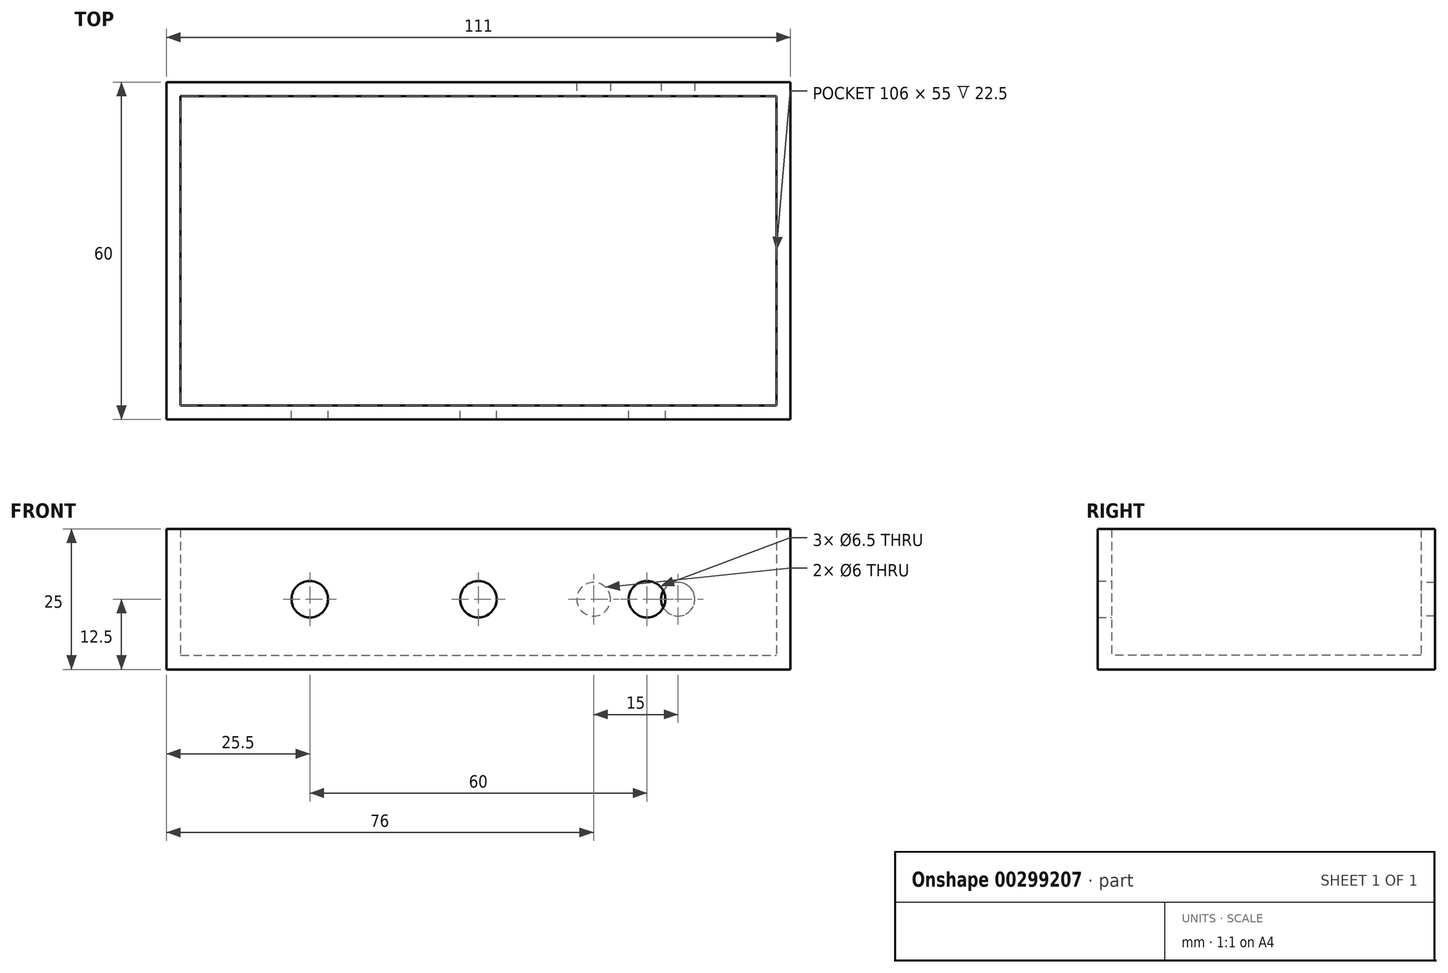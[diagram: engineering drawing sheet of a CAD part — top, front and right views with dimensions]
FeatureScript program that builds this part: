
annotation { "Feature Type Name" : "Feature", "Feature Type Description" : "" }
export const myFeature = defineFeature(function(context is Context, id is Id, definition is map)
    precondition{}
    {
        {
            var Q0;
            Q0=qCreatedBy(makeId("Top.planeOp"),FACE);
            var sketch = newSketch(context, id + "F0", { "sketchPlane" : qUnion([Q0])});
            skLineSegment(sketch, "E0.bottom", {"start": v(-55.5, 30) * mm, "end": v(55.5, 30) * mm});
            skLineSegment(sketch, "E0.top", {"start": v(-55.5, -30) * mm, "end": v(55.5, -30) * mm});
            skLineSegment(sketch, "E0.left", {"start": v(-55.5, 30) * mm, "end": v(-55.5, -30) * mm});
            skLineSegment(sketch, "E0.right", {"start": v(55.5, 30) * mm, "end": v(55.5, -30) * mm});
            skPoint(sketch, "E0.middle", {"position": v(0, 0) * mm});
            skSolve(sketch);
        }
        {
            var Q0;
            Q0 = qSketchRegion(id + "F0", true);
            extrude(context, id + "F1", {"entities" : qUnion([Q0]), "depth" : 25 * mm, "offsetDistance" : 25 * mm});
        }
        {
            var Q0;
            Q0=makeQuery(id+"F1.opExtrude","CAP_FACE",FACE,{"disambiguationData":[OSD([sQuery(id+"F0.wireOp",EDGE,"E0.bottom"),sQuery(id+"F0.wireOp",EDGE,"E0.top"),sQuery(id+"F0.wireOp",EDGE,"E0.left"),sQuery(id+"F0.wireOp",EDGE,"E0.right")])],"isStart":false});
            shell(context, id + "F2", {"entities" : qUnion([Q0]), "thickness" : 2.5 * mm});
        }
        {
            var Q0;
            Q0=qCreatedBy(makeId("Front.planeOp"),FACE);
            var sketch = newSketch(context, id + "F3", { "sketchPlane" : qUnion([Q0])});
            skCircle(sketch, "E1", {"center": v(-30, 12.5) * mm, "radius": 3.25 * mm});
            skCircle(sketch, "E2", {"center": v(30, 12.5) * mm, "radius": 3.25 * mm});
            skCircle(sketch, "E3", {"center": v(0, 12.5) * mm, "radius": 3.25 * mm});
            skSolve(sketch);
        }
        {
            var Q0;
            Q0 = qSketchRegion(id + "F3", true);
            var Q1;
            Q1=makeQuery(id+"F1.opExtrude","SWEPT_FACE",FACE,{"disambiguationData":[OSD([sQuery(id+"F0.wireOp",EDGE,"E0.top")])]});
            extrude(context, id + "F4", {"entities" : qUnion([Q0]), "operationType" : NewBodyOperationType.REMOVE, "endBound" : BoundingType.UP_TO_SURFACE, "depth" : 25 * mm, "endBoundEntityFace" : qUnion([Q1]), "offsetDistance" : 25 * mm});
        }
        {
            var Q0;
            Q0=qCreatedBy(makeId("Front.planeOp"),FACE);
            var sketch = newSketch(context, id + "F5", { "sketchPlane" : qUnion([Q0])});
            skCircle(sketch, "E4", {"center": v(20.5, 12.5) * mm, "radius": 3 * mm});
            skCircle(sketch, "E5", {"center": v(35.5, 12.5) * mm, "radius": 3 * mm});
            skSolve(sketch);
        }
        {
            var Q0;
            Q0 = qSketchRegion(id + "F5", true);
            var Q1;
            Q1=makeQuery(id+"F1.opExtrude","SWEPT_FACE",FACE,{"disambiguationData":[OSD([sQuery(id+"F0.wireOp",EDGE,"E0.bottom")])]});
            extrude(context, id + "F6", {"entities" : qUnion([Q0]), "operationType" : NewBodyOperationType.REMOVE, "endBound" : BoundingType.UP_TO_SURFACE, "oppositeDirection" : true, "depth" : 25 * mm, "endBoundEntityFace" : qUnion([Q1]), "offsetDistance" : 25 * mm});
        }
    });
